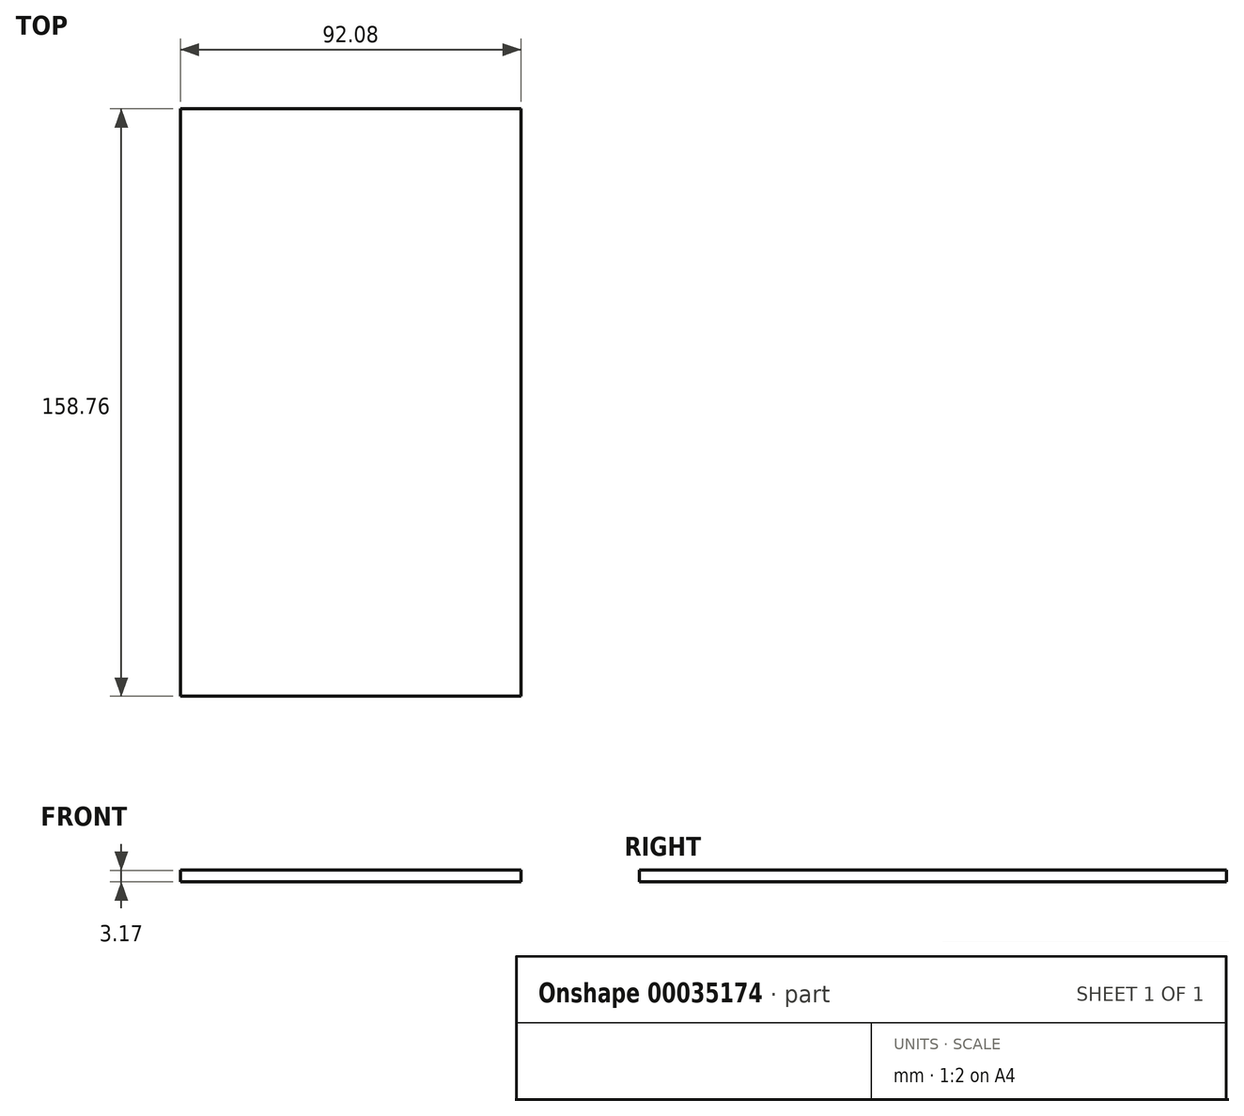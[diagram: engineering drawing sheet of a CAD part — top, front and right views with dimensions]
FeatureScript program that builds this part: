
annotation { "Feature Type Name" : "Feature", "Feature Type Description" : "" }
export const myFeature = defineFeature(function(context is Context, id is Id, definition is map)
    precondition{}
    {
        {
            var Q0;
            Q0=qCreatedBy(makeId("Top.planeOp"),FACE);
            var sketch = newSketch(context, id + "F0", { "sketchPlane" : qUnion([Q0])});
            skLineSegment(sketch, "E0.rect.bottom", {"start": v(46.04, 79.38) * mm, "end": v(-46.04, 79.38) * mm});
            skLineSegment(sketch, "E0.rect.top", {"start": v(46.04, -79.38) * mm, "end": v(-46.04, -79.38) * mm});
            skLineSegment(sketch, "E0.rect.left", {"start": v(46.04, 79.38) * mm, "end": v(46.04, -79.38) * mm});
            skLineSegment(sketch, "E0.rect.right", {"start": v(-46.04, 79.38) * mm, "end": v(-46.04, -79.38) * mm});
            skPoint(sketch, "E0.rect.middle", {"position": v(0, 0) * mm});
            skSolve(sketch);
        }
        {
            var Q0;
            Q0=makeQuery(id+"F0.imprint","IMPRINT",FACE,{"disambiguationData":[TD([[makeQuery(id+"F0.imprint","IMPRINT",EDGE,{"derivedFrom":sQuery(id+"F0.wireOp",EDGE,"E0.rect.bottom")}),1.0]])]});
            extrude(context, id + "F1", {"entities" : qUnion([Q0]), "depth" : 3.17 * mm});
        }
    });
